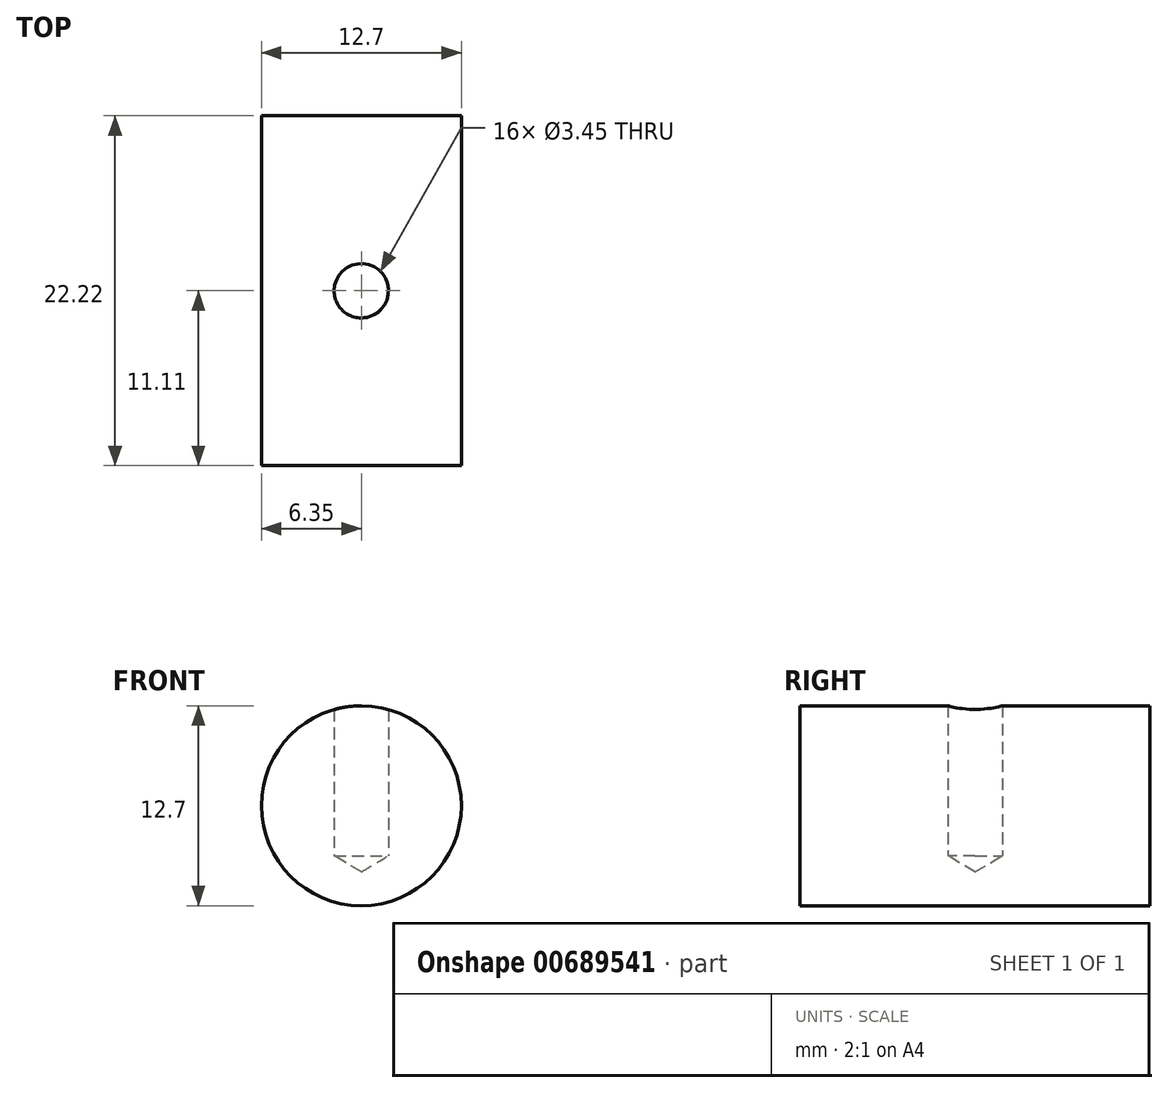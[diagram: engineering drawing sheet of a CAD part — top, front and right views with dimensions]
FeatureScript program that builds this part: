
annotation { "Feature Type Name" : "Feature", "Feature Type Description" : "" }
export const myFeature = defineFeature(function(context is Context, id is Id, definition is map)
    precondition{}
    {
        {
            var Q0;
            Q0=qCreatedBy(makeId("Front.planeOp"),FACE);
            var sketch = newSketch(context, id + "F0", { "sketchPlane" : qUnion([Q0])});
            skCircle(sketch, "E0", {"center": v(0, -6.35) * mm, "radius": 6.35 * mm});
            skPoint(sketch, "E1", {"position": v(0, 0) * mm});
            skSolve(sketch);
        }
        {
            var Q0;
            Q0 = qSketchRegion(id + "F0", true);
            extrude(context, id + "F1", {"entities" : qUnion([Q0]), "depth" : 22.22 * mm, "offsetDistance" : 25.4 * mm, "symmetric" : true});
        }
        {
            var Q0;
            Q0=qCreatedBy(makeId("Top.planeOp"),FACE);
            var sketch = newSketch(context, id + "F2", { "sketchPlane" : qUnion([Q0])});
            skPoint(sketch, "E2", {"position": v(0, 0) * mm});
            skSolve(sketch);
        }
        {
            var Q0;
            Q0=sQuery(id+"F2.wireOp",VERTEX,"E2");
            var Q1;
            Q1=makeQuery(id+"F1.opExtrude","SWEPT_BODY",BODY,{"disambiguationData":[OSD([sQuery(id+"F0.wireOp",EDGE,"E0")])]});
            hole(context, id + "F3", {"style" : HoleStyle.SIMPLE, "endStyle" : HoleEndStyle.BLIND, "standardTappedOrClearance" : lookupTablePath({ "standard" : "ANSI", "engagement" : "75%", "pitch" : "32 tpi", "size" : "#8", "type" : "Tapped" }), "standardBlindInLast" : lookupTablePath({ "standard" : "ANSI", "engagement" : "75%", "pitch" : "32 tpi", "size" : "#8", "type" : "Tapped" }), "holeDiameter" : 3.45 * mm, "majorDiameter" : 4.17 * mm, "showTappedDepth" : true, "holeDepth" : 9.52 * mm, "isTappedThrough" : true, "tappedDepth" : 7.14 * mm, "tapClearance" : 3, "locations" : qUnion([Q0]), "scope" : qUnion([Q1]), "startStyle" : HoleStartStyle.SKETCH});
        }
    });
